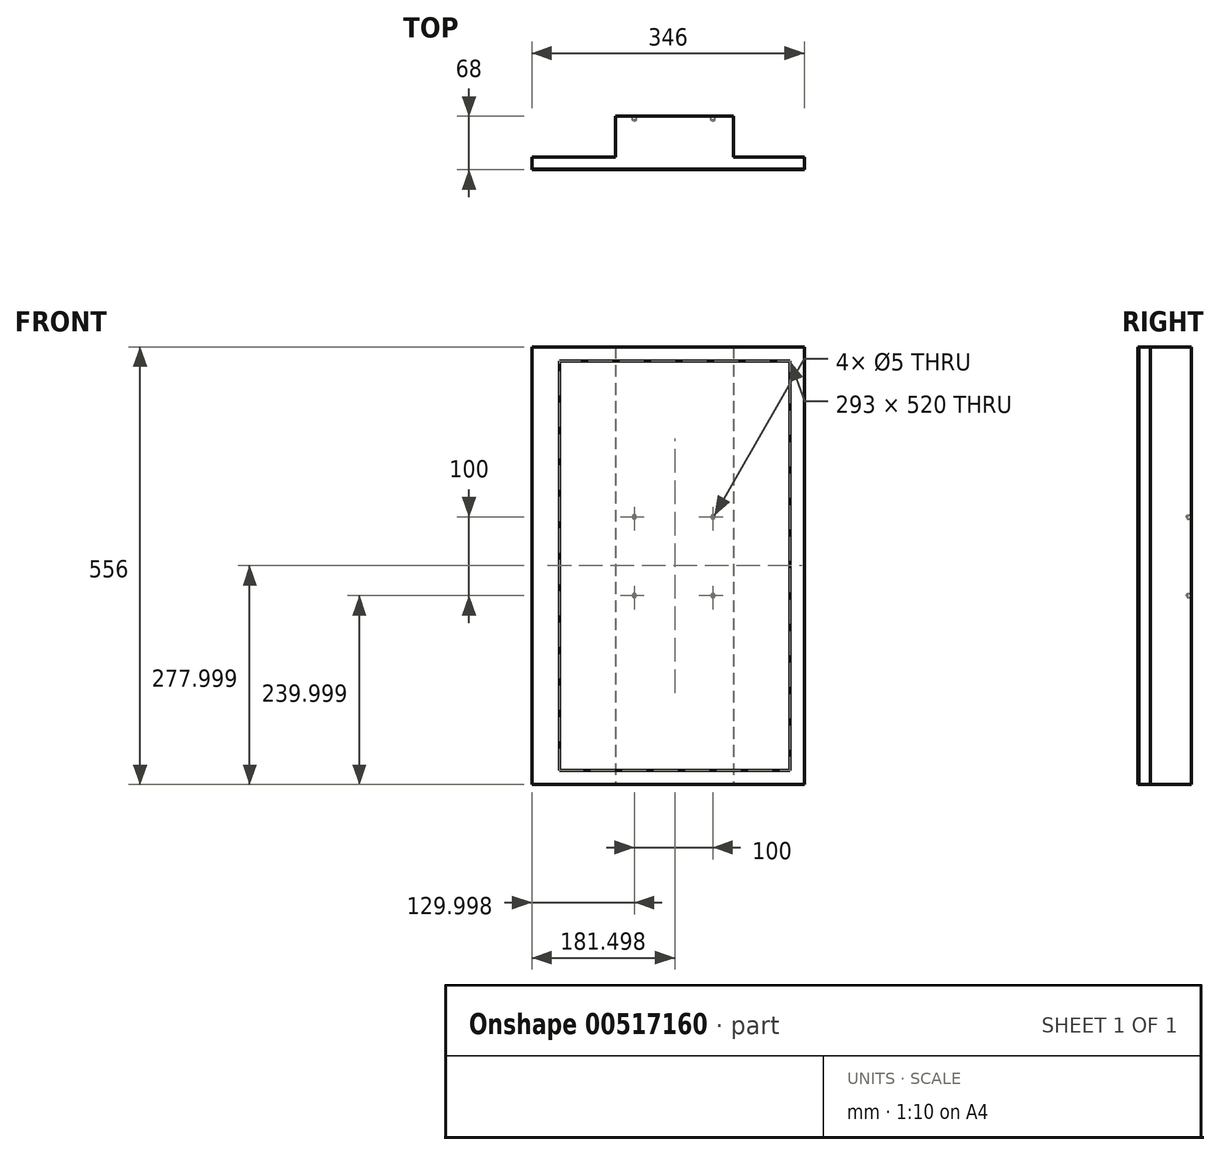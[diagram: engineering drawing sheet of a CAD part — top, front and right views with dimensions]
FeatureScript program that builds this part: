
annotation { "Feature Type Name" : "Feature", "Feature Type Description" : "" }
export const myFeature = defineFeature(function(context is Context, id is Id, definition is map)
    precondition{}
    {
        {
            assignVariable(context, id + "F0", {"name" : "mindepth", "anyValue" : 15});
        }
        {
            assignVariable(context, id + "F1", {"name" : "maxdepth", "anyValue" : 67});
        }
        {
            var Q0;
            Q0=qCreatedBy(makeId("Front.planeOp"),FACE);
            var sketch = newSketch(context, id + "F2", { "sketchPlane" : qUnion([Q0])});
            skLineSegment(sketch, "E0.bottom", {"start": v(-201, -247.88) * mm, "end": v(145, -247.88) * mm});
            skLineSegment(sketch, "E0.top", {"start": v(-201, 308.12) * mm, "end": v(145, 308.12) * mm});
            skLineSegment(sketch, "E0.left", {"start": v(-201, -247.88) * mm, "end": v(-201, 308.12) * mm});
            skLineSegment(sketch, "E0.right", {"start": v(145, -247.88) * mm, "end": v(145, 308.12) * mm});
            skSolve(sketch);
        }
        {
            var Q0;
            Q0=makeQuery(id+"F2.imprint","IMPRINT",FACE,{"disambiguationData":[TD([[makeQuery(id+"F2.imprint","IMPRINT",EDGE,{"derivedFrom":sQuery(id+"F2.wireOp",EDGE,"E0.bottom")}),1.0]])]});
            extrude(context, id + "F3", {"entities" : qUnion([Q0]), "oppositeDirection" : true, "depth" : (getVariable(context, 'mindepth')) * mm, "offsetDistance" : 25 * mm});
        }
        {
            var Q0;
            Q0=makeQuery(id+"F3.opExtrude","CAP_FACE",FACE,{"disambiguationData":[OSD([sQuery(id+"F2.wireOp",EDGE,"E0.bottom"),sQuery(id+"F2.wireOp",EDGE,"E0.top"),sQuery(id+"F2.wireOp",EDGE,"E0.left"),sQuery(id+"F2.wireOp",EDGE,"E0.right")])],"isStart":false});
            var sketch = newSketch(context, id + "F4", { "sketchPlane" : qUnion([Q0])});
            skLineSegment(sketch, "E1.bottom", {"start": v(-55, 308.12) * mm, "end": v(95, 308.12) * mm});
            skLineSegment(sketch, "E1.top", {"start": v(-55, -247.88) * mm, "end": v(95, -247.88) * mm});
            skLineSegment(sketch, "E1.left", {"start": v(-55, 308.12) * mm, "end": v(-55, -247.88) * mm});
            skLineSegment(sketch, "E1.right", {"start": v(95, 308.12) * mm, "end": v(95, -247.88) * mm});
            skSolve(sketch);
        }
        {
            var Q0;
            Q0=makeQuery(id+"F4.imprint","IMPRINT",FACE,{"disambiguationData":[TD([[makeQuery(id+"F4.imprint","IMPRINT",EDGE,{"derivedFrom":sQuery(id+"F4.wireOp",EDGE,"E1.bottom")}),1.0]])]});
            extrude(context, id + "F5", {"entities" : qUnion([Q0]), "operationType" : NewBodyOperationType.ADD, "depth" : (getVariable(context, 'maxdepth') - getVariable(context, 'mindepth')) * mm, "offsetDistance" : 25 * mm});
        }
        {
            var Q0;
            Q0=makeQuery(id+"F5.opExtrude","CAP_FACE",FACE,{"disambiguationData":[OSD([sQuery(id+"F4.wireOp",EDGE,"E1.bottom"),sQuery(id+"F4.wireOp",EDGE,"E1.top"),sQuery(id+"F4.wireOp",EDGE,"E1.left"),sQuery(id+"F4.wireOp",EDGE,"E1.right")])],"isStart":false});
            var sketch = newSketch(context, id + "F6", { "sketchPlane" : qUnion([Q0])});
            skLineSegment(sketch, "E2.bottom", {"start": v(-29, 92.12) * mm, "end": v(71, 92.12) * mm, "construction": true});
            skLineSegment(sketch, "E2.top", {"start": v(-29, -7.88) * mm, "end": v(71, -7.88) * mm, "construction": true});
            skLineSegment(sketch, "E2.left", {"start": v(-29, 92.12) * mm, "end": v(-29, -7.88) * mm, "construction": true});
            skLineSegment(sketch, "E2.right", {"start": v(71, 92.12) * mm, "end": v(71, -7.88) * mm, "construction": true});
            skPoint(sketch, "E3", {"position": v(-29, 92.12) * mm});
            skPoint(sketch, "E4", {"position": v(71, 92.12) * mm});
            skPoint(sketch, "E5", {"position": v(71, -7.88) * mm});
            skPoint(sketch, "E6", {"position": v(-29, -7.88) * mm});
            skSolve(sketch);
        }
        {
            var Q0;
            Q0=sQuery(id+"F6.wireOp",VERTEX,"E3");
            var Q1;
            Q1=sQuery(id+"F6.wireOp",VERTEX,"E4");
            var Q2;
            Q2=sQuery(id+"F6.wireOp",VERTEX,"E5");
            var Q3;
            Q3=sQuery(id+"F6.wireOp",VERTEX,"E6");
            var Q4;
            Q4=makeQuery(id+"F3.opExtrude","SWEPT_BODY",BODY,{"disambiguationData":[OSD([sQuery(id+"F2.wireOp",EDGE,"E0.bottom"),sQuery(id+"F2.wireOp",EDGE,"E0.top"),sQuery(id+"F2.wireOp",EDGE,"E0.left"),sQuery(id+"F2.wireOp",EDGE,"E0.right")])]});
            hole(context, id + "F7", {"style" : HoleStyle.SIMPLE, "endStyle" : HoleEndStyle.BLIND, "holeDiameter" : 5 * mm, "holeDepth" : 5 * mm, "isTappedThrough" : true, "tappedDepth" : 12 * mm, "tapClearance" : 3, "locations" : qUnion([Q0, Q1, Q2, Q3]), "scope" : qUnion([Q4])});
        }
        {
            var Q0;
            Q0=makeQuery(id+"F3.opExtrude","CAP_FACE",FACE,{"disambiguationData":[OSD([sQuery(id+"F2.wireOp",EDGE,"E0.bottom"),sQuery(id+"F2.wireOp",EDGE,"E0.top"),sQuery(id+"F2.wireOp",EDGE,"E0.left"),sQuery(id+"F2.wireOp",EDGE,"E0.right")])],"isStart":true});
            var sketch = newSketch(context, id + "F8", { "sketchPlane" : qUnion([Q0])});
            skLineSegment(sketch, "E7.bottom", {"start": v(-166, 290.12) * mm, "end": v(127, 290.12) * mm});
            skLineSegment(sketch, "E7.top", {"start": v(-166, -229.88) * mm, "end": v(127, -229.88) * mm});
            skLineSegment(sketch, "E7.left", {"start": v(-166, 290.12) * mm, "end": v(-166, -229.88) * mm});
            skLineSegment(sketch, "E7.right", {"start": v(127, 290.12) * mm, "end": v(127, -229.88) * mm});
            skSolve(sketch);
        }
        {
            var Q0;
            Q0=makeQuery(id+"F8.imprint","IMPRINT",FACE,{"disambiguationData":[TD([[makeQuery(id+"F8.imprint","IMPRINT",EDGE,{"derivedFrom":sQuery(id+"F8.wireOp",EDGE,"E7.bottom")}),1.0]])]});
            extrude(context, id + "F9", {"entities" : qUnion([Q0]), "depth" : 1 * mm, "offsetDistance" : 25 * mm});
        }
    });
